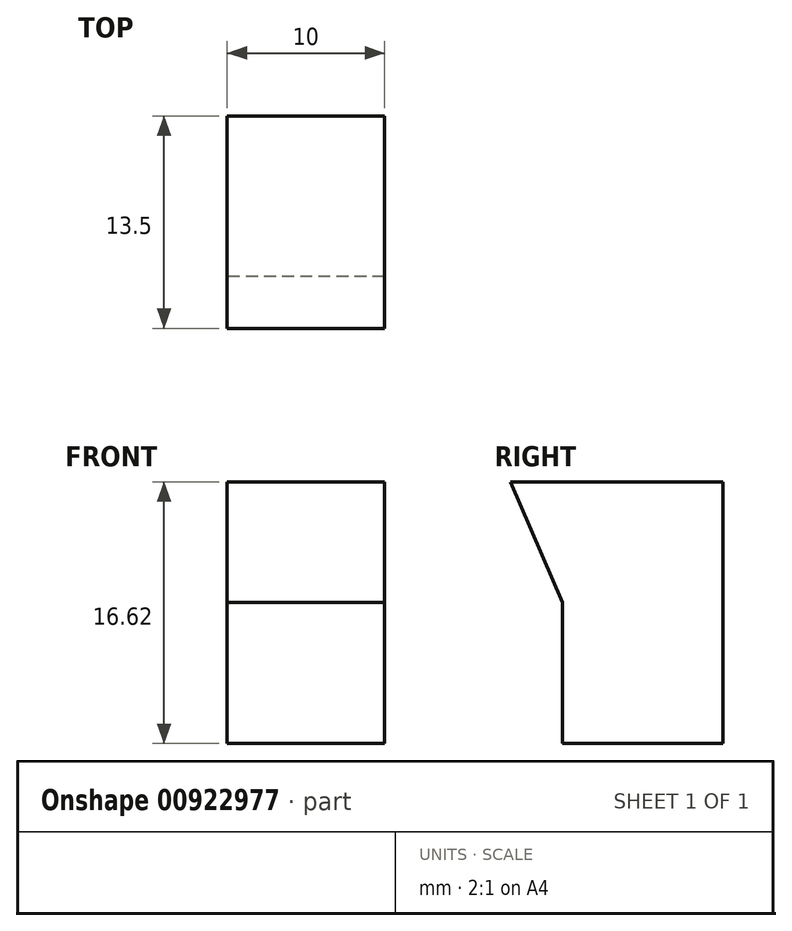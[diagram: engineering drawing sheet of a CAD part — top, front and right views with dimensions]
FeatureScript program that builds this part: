
annotation { "Feature Type Name" : "Feature", "Feature Type Description" : "" }
export const myFeature = defineFeature(function(context is Context, id is Id, definition is map)
    precondition{}
    {
        {
            var Q0;
            Q0=qCreatedBy(makeId("Right.planeOp"),FACE);
            var sketch = newSketch(context, id + "F0", { "sketchPlane" : qUnion([Q0])});
            skLineSegment(sketch, "E0", {"start": v(0, 0) * mm, "end": v(0, 16.62) * mm});
            skLineSegment(sketch, "E1", {"start": v(0, 16.62) * mm, "end": v(-13.5, 16.62) * mm});
            skLineSegment(sketch, "E2", {"start": v(-13.5, 16.62) * mm, "end": v(-10.2, 8.96) * mm});
            skLineSegment(sketch, "E3", {"start": v(-10.2, 8.96) * mm, "end": v(-10.2, 0) * mm});
            skLineSegment(sketch, "E4", {"start": v(-10.2, 0) * mm, "end": v(0, 0) * mm});
            skSolve(sketch);
        }
        {
            var Q0;
            Q0 = qSketchRegion(id + "F0", true);
            extrude(context, id + "F1", {"entities" : qUnion([Q0]), "depth" : 10 * mm, "offsetDistance" : 25 * mm});
        }
    });
